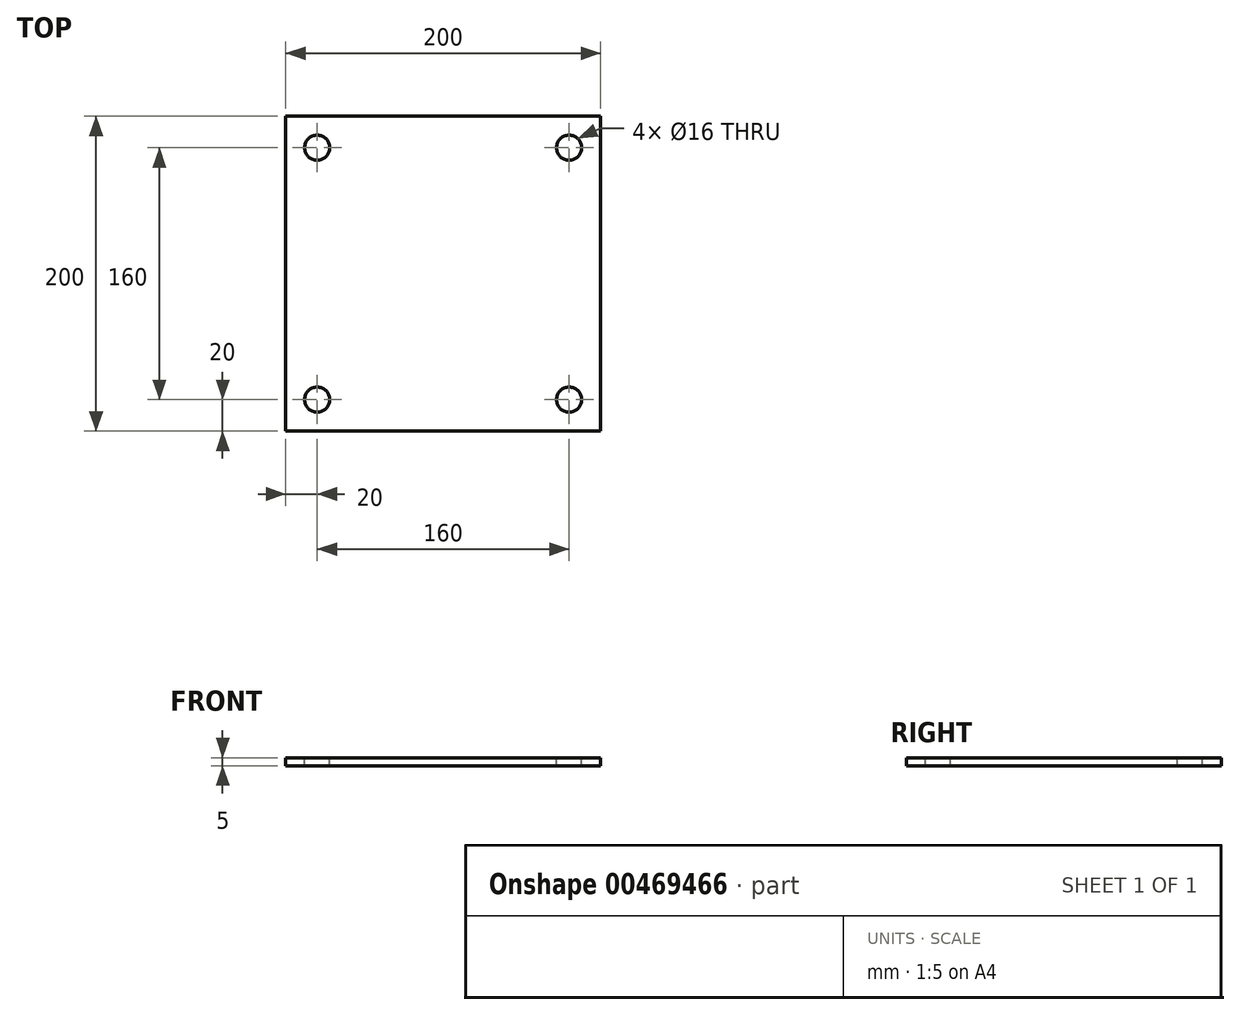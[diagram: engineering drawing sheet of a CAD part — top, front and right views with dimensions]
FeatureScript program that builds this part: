
annotation { "Feature Type Name" : "Feature", "Feature Type Description" : "" }
export const myFeature = defineFeature(function(context is Context, id is Id, definition is map)
    precondition{}
    {
        {
            var Q0;
            Q0=qCreatedBy(makeId("Top.planeOp"),FACE);
            var sketch = newSketch(context, id + "F0", { "sketchPlane" : qUnion([Q0])});
            skLineSegment(sketch, "E0.bottom", {"start": v(0, 0) * mm, "end": v(200, 0) * mm});
            skLineSegment(sketch, "E0.top", {"start": v(0, 200) * mm, "end": v(200, 200) * mm});
            skLineSegment(sketch, "E0.left", {"start": v(0, 0) * mm, "end": v(0, 200) * mm});
            skLineSegment(sketch, "E0.right", {"start": v(200, 0) * mm, "end": v(200, 200) * mm});
            skSolve(sketch);
        }
        {
            var Q0;
            Q0 = qSketchRegion(id + "F0", true);
            extrude(context, id + "F1", {"entities" : qUnion([Q0]), "depth" : 5 * mm});
        }
        {
            var Q0;
            Q0=makeQuery(id+"F1.opExtrude","CAP_FACE",FACE,{"disambiguationData":[OSD([sQuery(id+"F0.wireOp",EDGE,"E0.bottom"),sQuery(id+"F0.wireOp",EDGE,"E0.top"),sQuery(id+"F0.wireOp",EDGE,"E0.left"),sQuery(id+"F0.wireOp",EDGE,"E0.right")])],"isStart":false});
            var sketch = newSketch(context, id + "F2", { "sketchPlane" : qUnion([Q0])});
            skCircle(sketch, "E1", {"center": v(20, 180) * mm, "radius": 8 * mm});
            skCircle(sketch, "E2.MirrorC", {"center": v(180, 180) * mm, "radius": 8 * mm});
            skCircle(sketch, "E3.MirrorC", {"center": v(20, 20) * mm, "radius": 8 * mm});
            skCircle(sketch, "E4.MirrorC", {"center": v(180, 20) * mm, "radius": 8 * mm});
            skSolve(sketch);
        }
        {
            var Q0;
            Q0=sQuery(id+"F2.wireOp",VERTEX,"E4.MirrorC.center");
            var Q1;
            Q1=sQuery(id+"F2.wireOp",VERTEX,"E3.MirrorC.center");
            var Q2;
            Q2=sQuery(id+"F2.wireOp",VERTEX,"E2.MirrorC.center");
            var Q3;
            Q3=sQuery(id+"F2.wireOp",VERTEX,"E1.center");
            var Q4;
            Q4=makeQuery(id+"F1.opExtrude","SWEPT_BODY",BODY,{"disambiguationData":[OSD([sQuery(id+"F0.wireOp",EDGE,"E0.bottom"),sQuery(id+"F0.wireOp",EDGE,"E0.top"),sQuery(id+"F0.wireOp",EDGE,"E0.left"),sQuery(id+"F0.wireOp",EDGE,"E0.right")])]});
            hole(context, id + "F3", {"style" : HoleStyle.SIMPLE, "endStyle" : HoleEndStyle.THROUGH, "holeDiameter" : 16 * mm, "isTappedThrough" : true, "tappedDepth" : 12 * mm, "tapClearance" : 3, "startFromSketch" : true, "locations" : qUnion([Q0, Q1, Q2, Q3]), "scope" : qUnion([Q4])});
        }
    });
